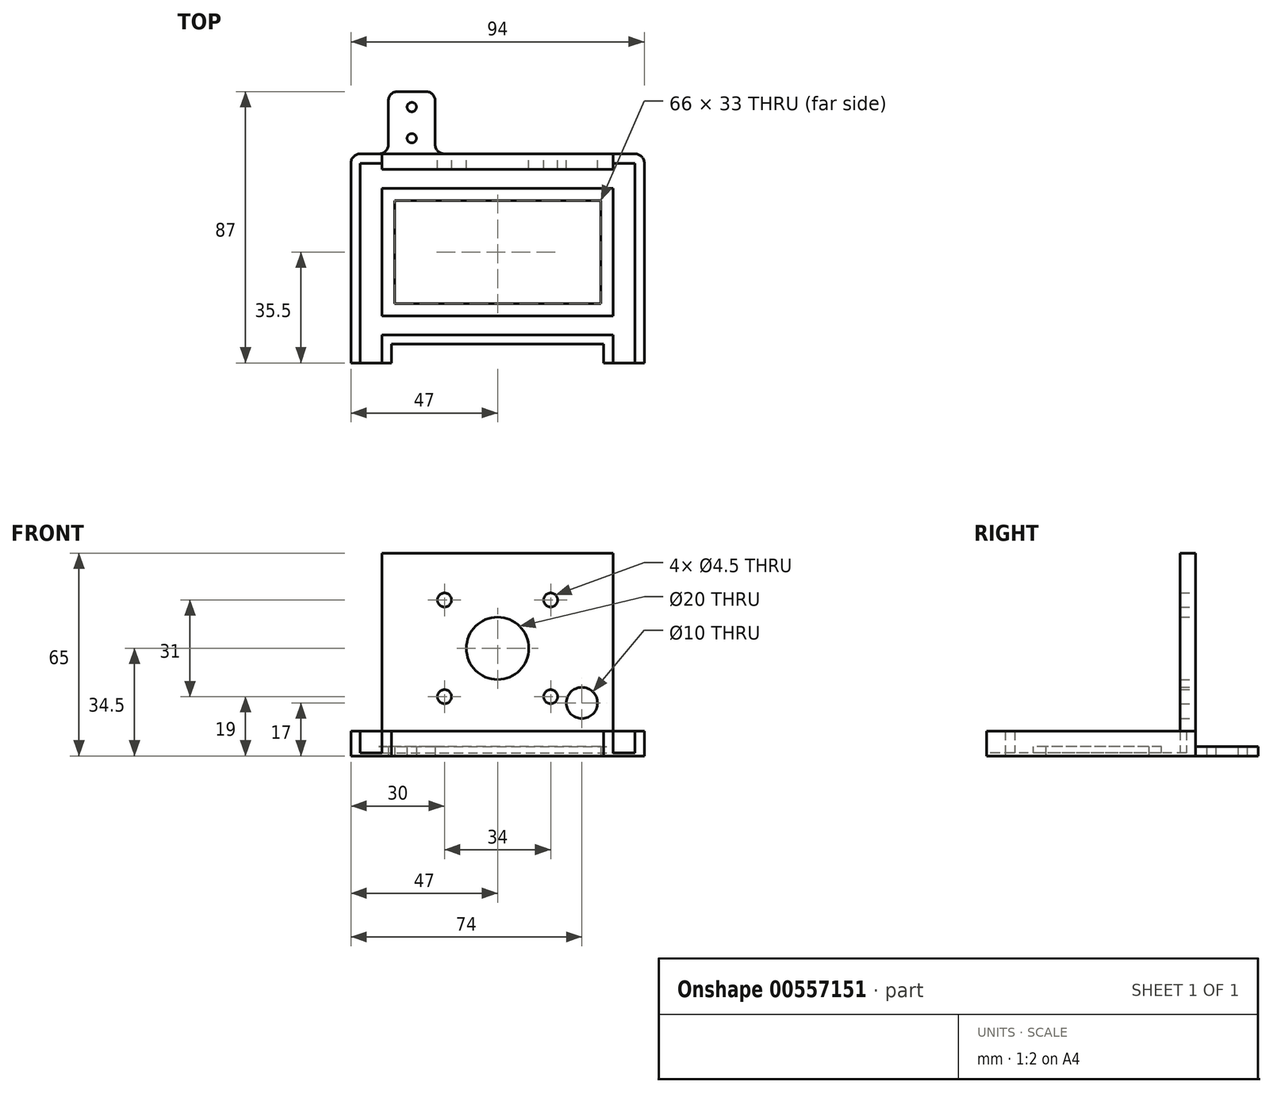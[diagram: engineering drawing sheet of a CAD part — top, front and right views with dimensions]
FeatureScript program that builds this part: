
annotation { "Feature Type Name" : "Feature", "Feature Type Description" : "" }
export const myFeature = defineFeature(function(context is Context, id is Id, definition is map)
    precondition{}
    {
        {
            var Q0;
            Q0=qCreatedBy(makeId("Top.planeOp"),FACE);
            var sketch = newSketch(context, id + "F0", { "sketchPlane" : qUnion([Q0])});
            skLineSegment(sketch, "E0.bottom", {"start": v(44, 32) * mm, "end": v(37, 32) * mm, "construction": true});
            skLineSegment(sketch, "E0.left", {"start": v(44, 32) * mm, "end": v(44, -32) * mm, "construction": true});
            skLineSegment(sketch, "E0.right", {"start": v(-44, 32) * mm, "end": v(-44, -32) * mm, "construction": true});
            skPoint(sketch, "E0.middle", {"position": v(0, 0) * mm});
            skLineSegment(sketch, "E1.0", {"start": v(47, 35) * mm, "end": v(-20, 35) * mm});
            skLineSegment(sketch, "E1.1", {"start": v(47, 35) * mm, "end": v(47, -32) * mm});
            skLineSegment(sketch, "E1.3", {"start": v(-47, 35) * mm, "end": v(-47, -32) * mm});
            skLineSegment(sketch, "E2.0", {"start": v(37, -23) * mm, "end": v(-37, -23) * mm, "construction": true});
            skLineSegment(sketch, "E3.0", {"start": v(-37, 24) * mm, "end": v(-37, -17) * mm, "construction": true});
            skLineSegment(sketch, "E3.2", {"start": v(37, 24) * mm, "end": v(37, -17) * mm, "construction": true});
            skLineSegment(sketch, "E4", {"start": v(-37, 32) * mm, "end": v(-37, 30) * mm, "construction": true});
            skLineSegment(sketch, "E5", {"start": v(-37, 30) * mm, "end": v(37, 30) * mm, "construction": true});
            skLineSegment(sketch, "E6", {"start": v(37, 30) * mm, "end": v(37, 32) * mm, "construction": true});
            skLineSegment(sketch, "E7.trimOffspring", {"start": v(-37, 32) * mm, "end": v(-44, 32) * mm, "construction": true});
            skLineSegment(sketch, "E8.0", {"start": v(-37, 24) * mm, "end": v(37, 24) * mm, "construction": true});
            skLineSegment(sketch, "E9", {"start": v(34, -32) * mm, "end": v(34, -26) * mm});
            skLineSegment(sketch, "E10", {"start": v(34, -26) * mm, "end": v(-34, -26) * mm});
            skLineSegment(sketch, "E11", {"start": v(-34, -26) * mm, "end": v(-34, -32) * mm});
            skLineSegment(sketch, "E12", {"start": v(-47, -32) * mm, "end": v(-34, -32) * mm});
            skLineSegment(sketch, "E13.trimOffspring", {"start": v(34, -32) * mm, "end": v(47, -32) * mm});
            skLineSegment(sketch, "E14.bottom", {"start": v(33, 20) * mm, "end": v(-33, 20) * mm});
            skLineSegment(sketch, "E14.left", {"start": v(33, 20) * mm, "end": v(33, -13) * mm});
            skLineSegment(sketch, "E14.right", {"start": v(-33, 20) * mm, "end": v(-33, -13) * mm});
            skLineSegment(sketch, "E15", {"start": v(-35, 35) * mm, "end": v(-35, 55) * mm});
            skLineSegment(sketch, "E16", {"start": v(-35, 55) * mm, "end": v(-20, 55) * mm});
            skLineSegment(sketch, "E17", {"start": v(-20, 55) * mm, "end": v(-20, 35) * mm});
            skLineSegment(sketch, "E18", {"start": v(-27.5, 55) * mm, "end": v(-27.5, 35) * mm, "construction": true});
            skCircle(sketch, "E19", {"center": v(-27.5, 50) * mm, "radius": 1.5 * mm});
            skCircle(sketch, "E20", {"center": v(-27.5, 40) * mm, "radius": 1.5 * mm});
            skLineSegment(sketch, "E21.trimOffspring", {"start": v(-35, 35) * mm, "end": v(-47, 35) * mm});
            skLineSegment(sketch, "E22", {"start": v(-37, -17) * mm, "end": v(37, -17) * mm, "construction": true});
            skPoint(sketch, "E23.orphan", {"position": v(-33, -20) * mm});
            skPoint(sketch, "E24.orphan", {"position": v(33, -20) * mm});
            skLineSegment(sketch, "E25.trimOffspring", {"start": v(-37, -23) * mm, "end": v(-37, -32) * mm, "construction": true});
            skLineSegment(sketch, "E26.trimOffspring", {"start": v(37, -23) * mm, "end": v(37, -32) * mm, "construction": true});
            skLineSegment(sketch, "E27.0", {"start": v(-33, -13) * mm, "end": v(33, -13) * mm});
            skSolve(sketch);
        }
        {
            var Q0;
            Q0 = qSketchRegion(id + "F0", true);
            extrude(context, id + "F1", {"entities" : qUnion([Q0]), "depth" : 3 * mm, "offsetDistance" : 25 * mm});
        }
        {
            var Q0;
            Q0=makeQuery(id+"F1.opExtrude","CAP_FACE",FACE,{"disambiguationData":[OSD([sQuery(id+"F0.wireOp",EDGE,"E1.0"),sQuery(id+"F0.wireOp",EDGE,"E1.1"),sQuery(id+"F0.wireOp",EDGE,"E1.3"),sQuery(id+"F0.wireOp",EDGE,"E9"),sQuery(id+"F0.wireOp",EDGE,"E10"),sQuery(id+"F0.wireOp",EDGE,"E11"),sQuery(id+"F0.wireOp",EDGE,"E12"),sQuery(id+"F0.wireOp",EDGE,"E13.trimOffspring"),sQuery(id+"F0.wireOp",EDGE,"E14.bottom"),sQuery(id+"F0.wireOp",EDGE,"E14.top"),sQuery(id+"F0.wireOp",EDGE,"E14.left"),sQuery(id+"F0.wireOp",EDGE,"E14.right"),sQuery(id+"F0.wireOp",EDGE,"E15"),sQuery(id+"F0.wireOp",EDGE,"E16"),sQuery(id+"F0.wireOp",EDGE,"E17"),sQuery(id+"F0.wireOp",EDGE,"E19"),sQuery(id+"F0.wireOp",EDGE,"E20"),sQuery(id+"F0.wireOp",EDGE,"E21.trimOffspring")])],"isStart":false});
            var sketch = newSketch(context, id + "F2", { "sketchPlane" : qUnion([Q0])});
            skLineSegment(sketch, "E28.0", {"start": v(-37, 30) * mm, "end": v(37, 30) * mm});
            skLineSegment(sketch, "E29.0", {"start": v(-37, 32) * mm, "end": v(-44, 32) * mm});
            skLineSegment(sketch, "E30.0", {"start": v(-44, 32) * mm, "end": v(-44, -32) * mm});
            skLineSegment(sketch, "E31.0", {"start": v(-37, 32) * mm, "end": v(-37, 30) * mm});
            skLineSegment(sketch, "E32.0", {"start": v(44, 32) * mm, "end": v(37, 32) * mm});
            skLineSegment(sketch, "E33.0", {"start": v(37, 30) * mm, "end": v(37, 32) * mm});
            skLineSegment(sketch, "E34.0", {"start": v(44, 32) * mm, "end": v(44, -32) * mm});
            skLineSegment(sketch, "E35.0", {"start": v(34, -26) * mm, "end": v(-34, -26) * mm});
            skLineSegment(sketch, "E36.0", {"start": v(37, -23) * mm, "end": v(-37, -23) * mm});
            skLineSegment(sketch, "E37.0", {"start": v(-47, -32) * mm, "end": v(-44, -32) * mm});
            skLineSegment(sketch, "E38.0", {"start": v(34, -32) * mm, "end": v(37, -32) * mm});
            skLineSegment(sketch, "E39.0", {"start": v(34, -32) * mm, "end": v(34, -26) * mm});
            skLineSegment(sketch, "E40.0", {"start": v(-34, -26) * mm, "end": v(-34, -32) * mm});
            skPoint(sketch, "E41.orphan", {"position": v(-37, 24) * mm});
            skPoint(sketch, "E42.orphan", {"position": v(37, 24) * mm});
            skLineSegment(sketch, "E43.trimOffspring", {"start": v(44, -32) * mm, "end": v(47, -32) * mm});
            skLineSegment(sketch, "E44.trimOffspring", {"start": v(-37, -32) * mm, "end": v(-34, -32) * mm});
            skLineSegment(sketch, "E45.0", {"start": v(-47, 35) * mm, "end": v(-47, -32) * mm});
            skLineSegment(sketch, "E46.0", {"start": v(47, 35) * mm, "end": v(47, -32) * mm});
            skLineSegment(sketch, "E47.0", {"start": v(47, 35) * mm, "end": v(-20, 35) * mm});
            skLineSegment(sketch, "E48.0", {"start": v(-35, 35) * mm, "end": v(-47, 35) * mm});
            skLineSegment(sketch, "E49", {"start": v(-35, 35) * mm, "end": v(-20, 35) * mm});
            skPoint(sketch, "E50.0.end.orphan", {"position": v(37, -17) * mm});
            skPoint(sketch, "E51.0.end.orphan", {"position": v(-37, -17) * mm});
            skLineSegment(sketch, "E52.0", {"start": v(-37, -23) * mm, "end": v(-37, -32) * mm});
            skLineSegment(sketch, "E53.0", {"start": v(37, -23) * mm, "end": v(37, -32) * mm});
            skSolve(sketch);
        }
        {
            var Q0;
            Q0=makeQuery(id+"F2.imprint","IMPRINT",FACE,{"disambiguationData":[TD([[makeQuery(id+"F2.imprint","IMPRINT",EDGE,{"derivedFrom":sQuery(id+"F2.wireOp",EDGE,"E35.0")}),-1.0]])]});
            var Q1;
            Q1=makeQuery(id+"F2.imprint","IMPRINT",FACE,{"disambiguationData":[TD([[makeQuery(id+"F2.imprint","IMPRINT",EDGE,{"derivedFrom":sQuery(id+"F2.wireOp",EDGE,"E28.0")}),1.0]])]});
            extrude(context, id + "F3", {"entities" : qUnion([Q0, Q1]), "operationType" : NewBodyOperationType.ADD, "depth" : 5 * mm, "offsetDistance" : 25 * mm});
        }
        {
            var Q0;
            {var subQ0=sQuery(id+"F0.wireOp",EDGE,"E13.trimOffspring");var subQ1=sQuery(id+"F0.wireOp",EDGE,"E12");var subQ2=sQuery(id+"F0.wireOp",EDGE,"E14.right");var subQ3=sQuery(id+"F0.wireOp",EDGE,"E27.0");var subQ4=sQuery(id+"F0.wireOp",EDGE,"E14.bottom");var subQ5=sQuery(id+"F0.wireOp",EDGE,"E14.left");Q0=makeQuery(id+"F3.boolean.opBoolean","SPLIT",FACE,{"disambiguationData":[TD([makeQuery(id+"F1.opExtrude","SWEPT_FACE",FACE,{"disambiguationData":[OSD([subQ1])]})])],"derivedFrom":makeQuery(id+"F1.opExtrude","CAP_FACE",FACE,{"disambiguationData":[OSD([sQuery(id+"F0.wireOp",EDGE,"E1.0"),sQuery(id+"F0.wireOp",EDGE,"E1.1"),sQuery(id+"F0.wireOp",EDGE,"E1.3"),sQuery(id+"F0.wireOp",EDGE,"E9"),sQuery(id+"F0.wireOp",EDGE,"E10"),sQuery(id+"F0.wireOp",EDGE,"E11"),subQ1,subQ0,subQ4,subQ5,subQ2,sQuery(id+"F0.wireOp",EDGE,"E15"),sQuery(id+"F0.wireOp",EDGE,"E16"),sQuery(id+"F0.wireOp",EDGE,"E17"),sQuery(id+"F0.wireOp",EDGE,"E19"),sQuery(id+"F0.wireOp",EDGE,"E20"),sQuery(id+"F0.wireOp",EDGE,"E21.trimOffspring"),subQ3])],"isStart":false})});}
            var sketch = newSketch(context, id + "F4", { "sketchPlane" : qUnion([Q0])});
            skLineSegment(sketch, "E54.0", {"start": v(-37, 24) * mm, "end": v(37, 24) * mm});
            skLineSegment(sketch, "E55.0", {"start": v(37, 24) * mm, "end": v(37, -17) * mm});
            skLineSegment(sketch, "E56.0", {"start": v(-37, -17) * mm, "end": v(37, -17) * mm});
            skLineSegment(sketch, "E57.0", {"start": v(-37, 24) * mm, "end": v(-37, -17) * mm});
            skLineSegment(sketch, "E58.0", {"start": v(37, -23) * mm, "end": v(-37, -23) * mm});
            skLineSegment(sketch, "E59.0", {"start": v(-37, -23) * mm, "end": v(-37, -32) * mm});
            skLineSegment(sketch, "E60.0", {"start": v(-44, 32) * mm, "end": v(-44, -32) * mm});
            skLineSegment(sketch, "E61.0", {"start": v(-37, 32) * mm, "end": v(-44, 32) * mm});
            skLineSegment(sketch, "E62.0", {"start": v(-37, 32) * mm, "end": v(-37, 30) * mm});
            skLineSegment(sketch, "E63.0", {"start": v(-37, 30) * mm, "end": v(37, 30) * mm});
            skLineSegment(sketch, "E64.0", {"start": v(44, 32) * mm, "end": v(37, 32) * mm, "construction": true});
            skLineSegment(sketch, "E65.0", {"start": v(37, 30) * mm, "end": v(37, 32) * mm});
            skLineSegment(sketch, "E66.0", {"start": v(44, 32) * mm, "end": v(44, -32) * mm});
            skLineSegment(sketch, "E67.0", {"start": v(37, -23) * mm, "end": v(37, -32) * mm});
            skLineSegment(sketch, "E68", {"start": v(-44, -32) * mm, "end": v(-37, -32) * mm});
            skLineSegment(sketch, "E69", {"start": v(37, -32) * mm, "end": v(44, -32) * mm});
            skSolve(sketch);
        }
        {
            var Q0;
            Q0=makeQuery(id+"F4.imprint","IMPRINT",FACE,{"disambiguationData":[TD([[makeQuery(id+"F4.imprint","IMPRINT",EDGE,{"derivedFrom":sQuery(id+"F4.wireOp",EDGE,"E54.0")}),1.0]])]});
            extrude(context, id + "F5", {"entities" : qUnion([Q0]), "operationType" : NewBodyOperationType.REMOVE, "oppositeDirection" : true, "depth" : 2 * mm, "offsetDistance" : 25 * mm});
        }
        {
            var Q0;
            Q0=makeQuery(id+"F3.opExtrude","CAP_FACE",FACE,{"disambiguationData":[OSD([sQuery(id+"F2.wireOp",EDGE,"E28.0"),sQuery(id+"F2.wireOp",EDGE,"E29.0"),sQuery(id+"F2.wireOp",EDGE,"E30.0"),sQuery(id+"F2.wireOp",EDGE,"E31.0"),sQuery(id+"F2.wireOp",EDGE,"E32.0"),sQuery(id+"F2.wireOp",EDGE,"E33.0"),sQuery(id+"F2.wireOp",EDGE,"E34.0"),sQuery(id+"F2.wireOp",EDGE,"E37.0"),sQuery(id+"F2.wireOp",EDGE,"E43.trimOffspring"),sQuery(id+"F2.wireOp",EDGE,"E45.0"),sQuery(id+"F2.wireOp",EDGE,"E46.0"),sQuery(id+"F2.wireOp",EDGE,"E47.0"),sQuery(id+"F2.wireOp",EDGE,"E48.0"),sQuery(id+"F2.wireOp",EDGE,"E49")])],"isStart":false});
            var sketch = newSketch(context, id + "F6", { "sketchPlane" : qUnion([Q0])});
            skLineSegment(sketch, "E70.bottom", {"start": v(-37, 30) * mm, "end": v(37, 30) * mm});
            skLineSegment(sketch, "E70.top", {"start": v(-37, 35) * mm, "end": v(37, 35) * mm});
            skLineSegment(sketch, "E70.left", {"start": v(-37, 30) * mm, "end": v(-37, 35) * mm});
            skLineSegment(sketch, "E70.right", {"start": v(37, 30) * mm, "end": v(37, 35) * mm});
            skSolve(sketch);
        }
        {
            var Q0;
            Q0 = qSketchRegion(id + "F6", true);
            extrude(context, id + "F7", {"entities" : qUnion([Q0]), "depth" : 57 * mm, "offsetDistance" : 25 * mm});
        }
        {
            var Q0;
            Q0=makeQuery(id+"F7.boolean.opBoolean","MERGE",FACE,{"derivedFrom":[makeQuery(id+"F3.boolean.opBoolean","MERGE",FACE,{"derivedFrom":[makeQuery(id+"F1.opExtrude","SWEPT_FACE",FACE,{"disambiguationData":[OSD([sQuery(id+"F0.wireOp",EDGE,"E1.0")])]}),makeQuery(id+"F1.opExtrude","SWEPT_FACE",FACE,{"disambiguationData":[OSD([sQuery(id+"F0.wireOp",EDGE,"E21.trimOffspring")])]}),makeQuery(id+"F3.opExtrude","SWEPT_FACE",FACE,{"disambiguationData":[OSD([sQuery(id+"F2.wireOp",EDGE,"E47.0"),sQuery(id+"F2.wireOp",EDGE,"E48.0"),sQuery(id+"F2.wireOp",EDGE,"E49")])]})]}),makeQuery(id+"F7.opExtrude","SWEPT_FACE",FACE,{"disambiguationData":[OSD([sQuery(id+"F6.wireOp",EDGE,"E70.top")])]})]});
            var sketch = newSketch(context, id + "F8", { "sketchPlane" : qUnion([Q0])});
            skCircle(sketch, "E71", {"center": v(0, 34.5) * mm, "radius": 10 * mm});
            skCircle(sketch, "E72", {"center": v(-27, 17) * mm, "radius": 5 * mm});
            skCircle(sketch, "E73", {"center": v(-17, 50) * mm, "radius": 2.25 * mm});
            skLineSegment(sketch, "E74", {"start": v(0, 0) * mm, "end": v(0, 65) * mm, "construction": true});
            skLineSegment(sketch, "E75", {"start": v(0, 34.5) * mm, "end": v(-26.1, 34.5) * mm, "construction": true});
            skCircle(sketch, "E76.MirrorC", {"center": v(-17, 19) * mm, "radius": 2.25 * mm});
            skCircle(sketch, "E77.MirrorC", {"center": v(17, 19) * mm, "radius": 2.25 * mm});
            skCircle(sketch, "E78.MirrorC", {"center": v(17, 50) * mm, "radius": 2.25 * mm});
            skSolve(sketch);
        }
        {
            var Q0;
            Q0 = qSketchRegion(id + "F8", true);
            extrude(context, id + "F9", {"entities" : qUnion([Q0]), "operationType" : NewBodyOperationType.REMOVE, "endBound" : BoundingType.THROUGH_ALL, "oppositeDirection" : true, "depth" : 25 * mm, "offsetDistance" : 25 * mm});
        }
        {
            var Q0;
            Q0=makeQuery(id+"F1.opExtrude","SWEPT_EDGE",EDGE,{"disambiguationData":[OSD([sQuery(id+"F0.wireOp",EDGE,"E15"),sQuery(id+"F0.wireOp",EDGE,"E21.trimOffspring")])]});
            var Q1;
            Q1=makeQuery(id+"F1.opExtrude","SWEPT_EDGE",EDGE,{"disambiguationData":[OSD([sQuery(id+"F0.wireOp",EDGE,"E1.0"),sQuery(id+"F0.wireOp",EDGE,"E17")])]});
            var Q2;
            Q2=makeQuery(id+"F1.opExtrude","SWEPT_EDGE",EDGE,{"disambiguationData":[OSD([sQuery(id+"F0.wireOp",EDGE,"E15"),sQuery(id+"F0.wireOp",EDGE,"E16")])]});
            var Q3;
            Q3=makeQuery(id+"F1.opExtrude","SWEPT_EDGE",EDGE,{"disambiguationData":[OSD([sQuery(id+"F0.wireOp",EDGE,"E16"),sQuery(id+"F0.wireOp",EDGE,"E17")])]});
            var Q4;
            Q4=makeQuery(id+"F3.boolean.opBoolean","MERGE",EDGE,{"derivedFrom":[makeQuery(id+"F1.opExtrude","SWEPT_EDGE",EDGE,{"disambiguationData":[OSD([sQuery(id+"F0.wireOp",EDGE,"E1.3"),sQuery(id+"F0.wireOp",EDGE,"E21.trimOffspring")])]}),makeQuery(id+"F3.opExtrude","SWEPT_EDGE",EDGE,{"disambiguationData":[OSD([sQuery(id+"F2.wireOp",EDGE,"E45.0"),sQuery(id+"F2.wireOp",EDGE,"E48.0")])]})]});
            var Q5;
            Q5=makeQuery(id+"F3.boolean.opBoolean","MERGE",EDGE,{"derivedFrom":[makeQuery(id+"F1.opExtrude","SWEPT_EDGE",EDGE,{"disambiguationData":[OSD([sQuery(id+"F0.wireOp",EDGE,"E1.0"),sQuery(id+"F0.wireOp",EDGE,"E1.1")])]}),makeQuery(id+"F3.opExtrude","SWEPT_EDGE",EDGE,{"disambiguationData":[OSD([sQuery(id+"F2.wireOp",EDGE,"E46.0"),sQuery(id+"F2.wireOp",EDGE,"E47.0")])]})]});
            fillet(context, id + "F10", {"entities" : qUnion([Q0, Q1, Q2, Q3, Q4, Q5]), "radius" : 3 * mm, "tangentPropagation" : true, "allowEdgeOverflow" : false});
        }
    });
